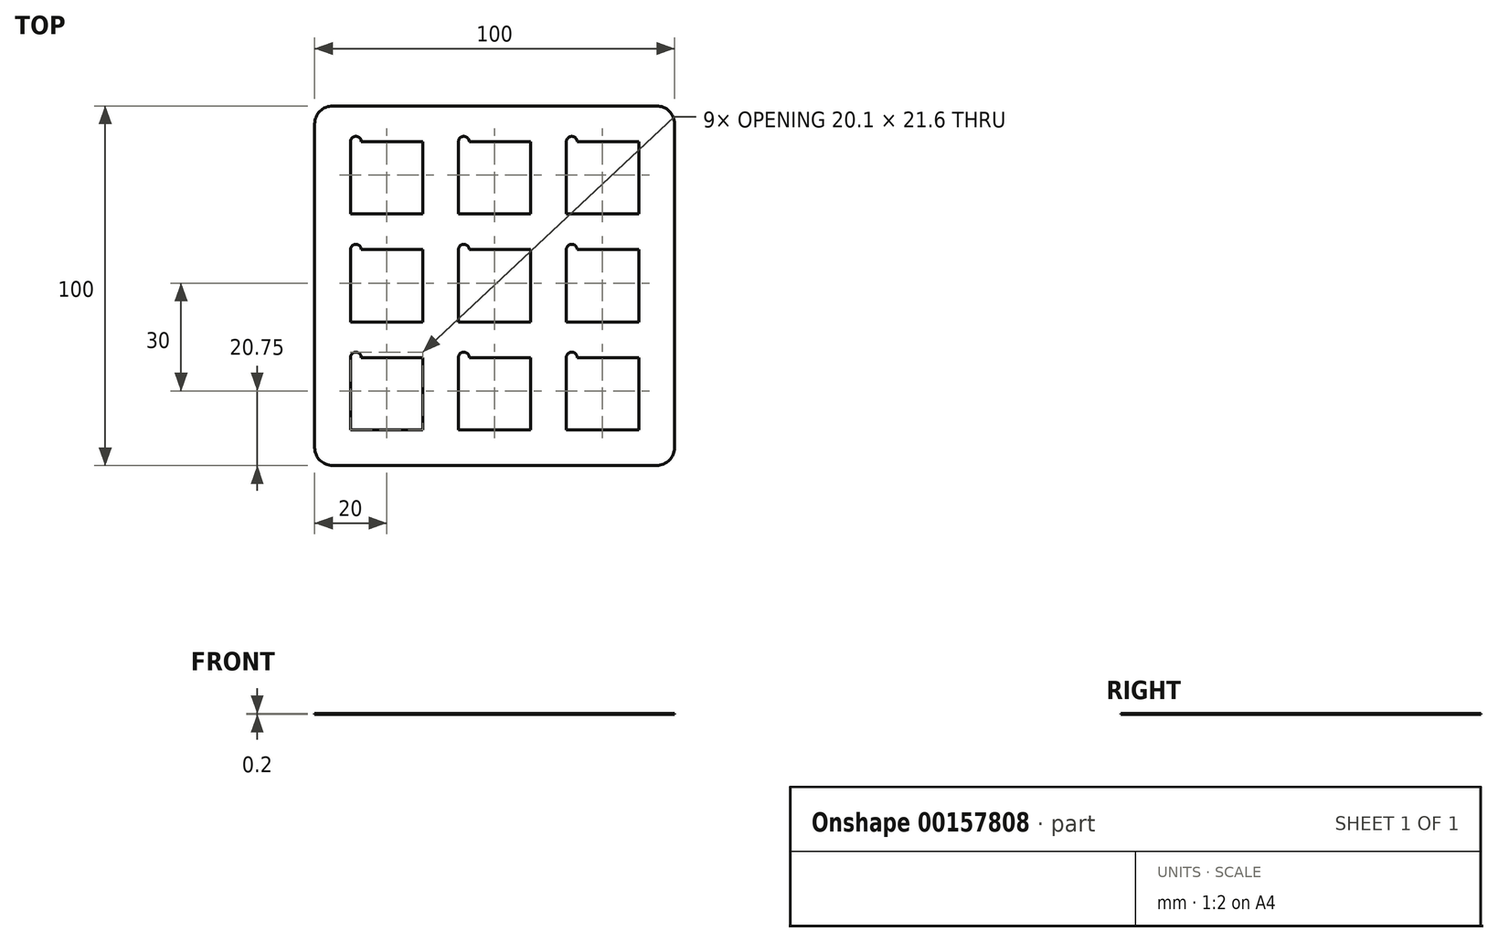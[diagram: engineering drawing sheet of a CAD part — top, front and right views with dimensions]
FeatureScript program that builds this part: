
annotation { "Feature Type Name" : "Feature", "Feature Type Description" : "" }
export const myFeature = defineFeature(function(context is Context, id is Id, definition is map)
    precondition{}
    {
        {
            var Q0;
            Q0=qCreatedBy(makeId("Top.planeOp"),FACE);
            var sketch = newSketch(context, id + "F0", { "sketchPlane" : qUnion([Q0])});
            skLineSegment(sketch, "E0.bottom", {"start": v(45, -50) * mm, "end": v(-45, -50) * mm});
            skLineSegment(sketch, "E0.top", {"start": v(45, 50) * mm, "end": v(-45, 50) * mm});
            skLineSegment(sketch, "E0.left", {"start": v(50, -45) * mm, "end": v(50, 45) * mm});
            skLineSegment(sketch, "E0.right", {"start": v(-50, -45) * mm, "end": v(-50, 45) * mm});
            skPoint(sketch, "E1.visualSharp", {"position": v(-50, 50) * mm});
            skArc(sketch, "E1.filletArc", {"start": v(-45, 50) * mm, "mid": v(-48.54, 48.54) * mm, "end": v(-50, 45) * mm});
            skPoint(sketch, "E2.visualSharp", {"position": v(50, 50) * mm});
            skArc(sketch, "E2.filletArc", {"start": v(50, 45) * mm, "mid": v(48.54, 48.54) * mm, "end": v(45, 50) * mm});
            skPoint(sketch, "E3.visualSharp", {"position": v(50, -50) * mm});
            skArc(sketch, "E3.filletArc", {"start": v(45, -50) * mm, "mid": v(48.54, -48.54) * mm, "end": v(50, -45) * mm});
            skPoint(sketch, "E4.visualSharp", {"position": v(-50, -50) * mm});
            skArc(sketch, "E4.filletArc", {"start": v(-50, -45) * mm, "mid": v(-48.54, -48.54) * mm, "end": v(-45, -50) * mm});
            skLineSegment(sketch, "E5", {"start": v(-30, 63.69) * mm, "end": v(-30, -63.96) * mm, "construction": true});
            skLineSegment(sketch, "E6", {"start": v(0, 63.69) * mm, "end": v(0, -63.96) * mm, "construction": true});
            skLineSegment(sketch, "E7", {"start": v(30, 63.69) * mm, "end": v(30, -63.96) * mm, "construction": true});
            skLineSegment(sketch, "E8", {"start": v(-59.25, 30) * mm, "end": v(61.2, 30) * mm, "construction": true});
            skLineSegment(sketch, "E9", {"start": v(61.2, 0) * mm, "end": v(-59.25, 0) * mm, "construction": true});
            skLineSegment(sketch, "E10", {"start": v(61.2, -30) * mm, "end": v(-59.25, -30) * mm, "construction": true});
            skLineSegment(sketch, "E11.bottom", {"start": v(-19.95, 19.95) * mm, "end": v(-40.05, 19.95) * mm});
            skLineSegment(sketch, "E11.top", {"start": v(-19.95, 40.05) * mm, "end": v(-37.05, 40.05) * mm});
            skLineSegment(sketch, "E11.left", {"start": v(-19.95, 19.95) * mm, "end": v(-19.95, 40.05) * mm});
            skLineSegment(sketch, "E11.right", {"start": v(-40.05, 19.95) * mm, "end": v(-40.05, 40.05) * mm});
            skArc(sketch, "E12", {"start": v(-37.05, 40.05) * mm, "mid": v(-38.55, 41.55) * mm, "end": v(-40.05, 40.05) * mm});
            skLineSegment(sketch, "E13.direction1", {"start": v(-40.05, 19.95) * mm, "end": v(-10.05, 19.95) * mm, "construction": true});
            skLineSegment(sketch, "E14.0.1.0", {"start": v(-19.95, 10.05) * mm, "end": v(-37.05, 10.05) * mm});
            skArc(sketch, "E14.0.1.1", {"start": v(-37.05, 10.05) * mm, "mid": v(-38.55, 11.55) * mm, "end": v(-40.05, 10.05) * mm});
            skLineSegment(sketch, "E14.0.1.2", {"start": v(-19.95, -10.05) * mm, "end": v(-40.05, -10.05) * mm});
            skLineSegment(sketch, "E14.0.1.3", {"start": v(-19.95, -10.05) * mm, "end": v(-19.95, 10.05) * mm});
            skLineSegment(sketch, "E14.0.1.4", {"start": v(-40.05, -10.05) * mm, "end": v(-40.05, 10.05) * mm});
            skLineSegment(sketch, "E14.0.2.0", {"start": v(-19.95, -19.95) * mm, "end": v(-37.05, -19.95) * mm});
            skArc(sketch, "E14.0.2.1", {"start": v(-37.05, -19.95) * mm, "mid": v(-38.55, -18.45) * mm, "end": v(-40.05, -19.95) * mm});
            skLineSegment(sketch, "E14.0.2.2", {"start": v(-19.95, -40.05) * mm, "end": v(-40.05, -40.05) * mm});
            skLineSegment(sketch, "E14.0.2.3", {"start": v(-19.95, -40.05) * mm, "end": v(-19.95, -19.95) * mm});
            skLineSegment(sketch, "E14.0.2.4", {"start": v(-40.05, -40.05) * mm, "end": v(-40.05, -19.95) * mm});
            skLineSegment(sketch, "E14.1.0.0", {"start": v(10.05, 40.05) * mm, "end": v(-7.05, 40.05) * mm});
            skArc(sketch, "E14.1.0.1", {"start": v(-7.05, 40.05) * mm, "mid": v(-8.55, 41.55) * mm, "end": v(-10.05, 40.05) * mm});
            skLineSegment(sketch, "E14.1.0.2", {"start": v(10.05, 19.95) * mm, "end": v(-10.05, 19.95) * mm});
            skLineSegment(sketch, "E14.1.0.3", {"start": v(10.05, 19.95) * mm, "end": v(10.05, 40.05) * mm});
            skLineSegment(sketch, "E14.1.0.4", {"start": v(-10.05, 19.95) * mm, "end": v(-10.05, 40.05) * mm});
            skLineSegment(sketch, "E14.1.1.0", {"start": v(10.05, 10.05) * mm, "end": v(-7.05, 10.05) * mm});
            skArc(sketch, "E14.1.1.1", {"start": v(-7.05, 10.05) * mm, "mid": v(-8.55, 11.55) * mm, "end": v(-10.05, 10.05) * mm});
            skLineSegment(sketch, "E14.1.1.2", {"start": v(10.05, -10.05) * mm, "end": v(-10.05, -10.05) * mm});
            skLineSegment(sketch, "E14.1.1.3", {"start": v(10.05, -10.05) * mm, "end": v(10.05, 10.05) * mm});
            skLineSegment(sketch, "E14.1.1.4", {"start": v(-10.05, -10.05) * mm, "end": v(-10.05, 10.05) * mm});
            skLineSegment(sketch, "E14.1.2.0", {"start": v(10.05, -19.95) * mm, "end": v(-7.05, -19.95) * mm});
            skArc(sketch, "E14.1.2.1", {"start": v(-7.05, -19.95) * mm, "mid": v(-8.55, -18.45) * mm, "end": v(-10.05, -19.95) * mm});
            skLineSegment(sketch, "E14.1.2.2", {"start": v(10.05, -40.05) * mm, "end": v(-10.05, -40.05) * mm});
            skLineSegment(sketch, "E14.1.2.3", {"start": v(10.05, -40.05) * mm, "end": v(10.05, -19.95) * mm});
            skLineSegment(sketch, "E14.1.2.4", {"start": v(-10.05, -40.05) * mm, "end": v(-10.05, -19.95) * mm});
            skLineSegment(sketch, "E14.2.0.0", {"start": v(40.05, 40.05) * mm, "end": v(22.95, 40.05) * mm});
            skArc(sketch, "E14.2.0.1", {"start": v(22.95, 40.05) * mm, "mid": v(21.45, 41.55) * mm, "end": v(19.95, 40.05) * mm});
            skLineSegment(sketch, "E14.2.0.2", {"start": v(40.05, 19.95) * mm, "end": v(19.95, 19.95) * mm});
            skLineSegment(sketch, "E14.2.0.3", {"start": v(40.05, 19.95) * mm, "end": v(40.05, 40.05) * mm});
            skLineSegment(sketch, "E14.2.0.4", {"start": v(19.95, 19.95) * mm, "end": v(19.95, 40.05) * mm});
            skLineSegment(sketch, "E14.2.1.0", {"start": v(40.05, 10.05) * mm, "end": v(22.95, 10.05) * mm});
            skArc(sketch, "E14.2.1.1", {"start": v(22.95, 10.05) * mm, "mid": v(21.45, 11.55) * mm, "end": v(19.95, 10.05) * mm});
            skLineSegment(sketch, "E14.2.1.2", {"start": v(40.05, -10.05) * mm, "end": v(19.95, -10.05) * mm});
            skLineSegment(sketch, "E14.2.1.3", {"start": v(40.05, -10.05) * mm, "end": v(40.05, 10.05) * mm});
            skLineSegment(sketch, "E14.2.1.4", {"start": v(19.95, -10.05) * mm, "end": v(19.95, 10.05) * mm});
            skLineSegment(sketch, "E14.2.2.0", {"start": v(40.05, -19.95) * mm, "end": v(22.95, -19.95) * mm});
            skArc(sketch, "E14.2.2.1", {"start": v(22.95, -19.95) * mm, "mid": v(21.45, -18.45) * mm, "end": v(19.95, -19.95) * mm});
            skLineSegment(sketch, "E14.2.2.2", {"start": v(40.05, -40.05) * mm, "end": v(19.95, -40.05) * mm});
            skLineSegment(sketch, "E14.2.2.3", {"start": v(40.05, -40.05) * mm, "end": v(40.05, -19.95) * mm});
            skLineSegment(sketch, "E14.2.2.4", {"start": v(19.95, -40.05) * mm, "end": v(19.95, -19.95) * mm});
            skLineSegment(sketch, "E14.direction2", {"start": v(-40.05, 19.95) * mm, "end": v(-40.05, -10.05) * mm, "construction": true});
            skSolve(sketch);
        }
        {
            var Q0;
            Q0 = qSketchRegion(id + "F0", true);
            extrude(context, id + "F1", {"entities" : qUnion([Q0]), "depth" : 0.2 * mm});
        }
    });
